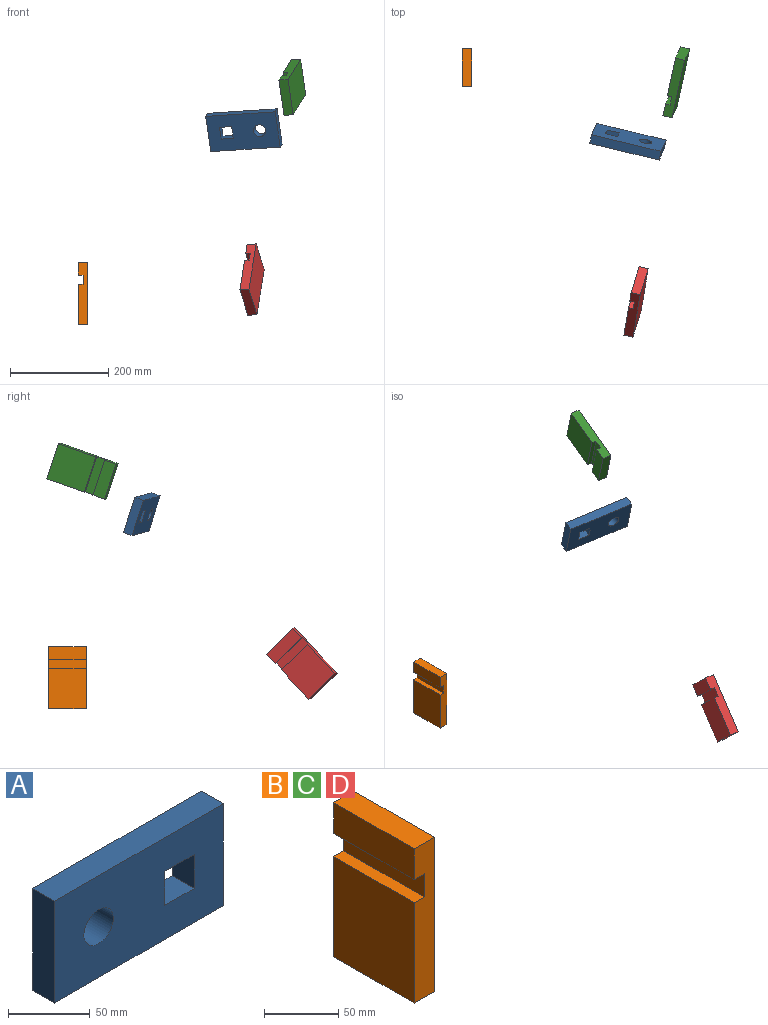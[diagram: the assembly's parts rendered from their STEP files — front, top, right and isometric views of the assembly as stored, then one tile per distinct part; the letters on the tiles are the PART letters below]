
ASSEMBLY  parts=4 mates=3
PART A: 11 faces, bbox 146.1x19.1x76.2 mm
  f0: plane 76.2x19.05mm, normal (-1,0,0), area 1451.6mm2, adj f1,f3,f4,f5
  f1: plane 146.05x19.05mm, normal (0,0,-1), area 2782.3mm2, adj f0,f2,f4,f5
  f2: plane 76.2x19.05mm, normal (1,0,0), area 1451.6mm2, adj f1,f3,f4,f5
  f3: plane 146.05x19.05mm, normal (0,0,1), area 2782.3mm2, adj f0,f2,f4,f5
  f4: plane 146.05x76.2mm, normal (0,-1,0), area 9977.1mm2, adj f0,f1,f2,f3,f6,f7,f8,f9
  f5: plane 146.05x76.2mm, normal (0,1,0), area 9977.1mm2, adj f0,f1,f2,f3,f6,f7,f8,f9
  f6: plane 25.4x19.05mm, normal (1,0,0), area 483.9mm2, adj f4,f5,f7,f9
  f7: plane 25.4x19.05mm, normal (0,0,1), area 483.9mm2, adj f4,f5,f6,f8
  f8: plane 25.4x19.05mm, normal (-1,0,0), area 483.9mm2, adj f4,f5,f7,f9
  f9: plane 25.4x19.05mm, normal (0,0,-1), area 483.9mm2, adj f4,f5,f6,f8
  f10: cylinder r=12.7mm len=25.4mm, axis (0,-1,0), area 1520.1mm2, adj f4,f5
PART B: 10 faces, bbox 19.1x76.2x127 mm
  f0: plane 82.55x76.2mm, normal (-1,0,0), area 6290.3mm2, adj f1,f7,f8,f9
  f1: plane 76.2x19.05mm, normal (0,0,-1), area 1451.6mm2, adj f0,f2,f8,f9
  f2: plane 127x76.2mm, normal (1,0,0), area 9677.4mm2, adj f1,f3,f8,f9
  f3: plane 76.2x19.05mm, normal (0,0,1), area 1451.6mm2, adj f2,f4,f8,f9
  f4: plane 76.2x25.4mm, normal (-1,0,0), area 1935.5mm2, adj f3,f5,f8,f9
  f5: plane 76.2x9.53mm, normal (0,0,-1), area 725.8mm2, adj f4,f6,f8,f9
  f6: plane 76.2x19.05mm, normal (-1,0,0), area 1451.6mm2, adj f5,f7,f8,f9
  f7: plane 76.2x9.53mm, normal (0,0,1), area 725.8mm2, adj f0,f6,f8,f9
  f8: plane 127x19.05mm, normal (0,-1,0), area 2237.9mm2, adj f0,f1,f2,f3,f4,f5,f6,f7
  f9: plane 127x19.05mm, normal (0,1,0), area 2237.9mm2, adj f0,f1,f2,f3,f4,f5,f6,f7
PART C: same geometry as B
PART D: same geometry as B
PLACE A rot(axis=(0.11,0.98,0.16),174.2deg) t=(426.64,-61.9,39.15)mm
PLACE B t=(107.06,138.74,-433.83)mm
PLACE C rot(axis=(0.99,-0.14,-0.05),109.3deg) t=(547.39,139.97,156.21)mm
PLACE D rot(axis=(-0.95,0.04,-0.31),45.9deg) t=(447.43,-426.5,-401.64)mm
MATE planar A.f0 <-> C.f6  axis (0.97,-0.23,0.06) through (467.69,-68.21,2.61)mm
MATE planar D.f6 <-> A.f0  axis (-0.97,0.23,-0.06) through (416.75,-358.09,-286)mm
MATE planar C.f6 <-> A.f0  axis (-0.97,0.23,-0.06) through (489.81,43.54,76.35)mm
